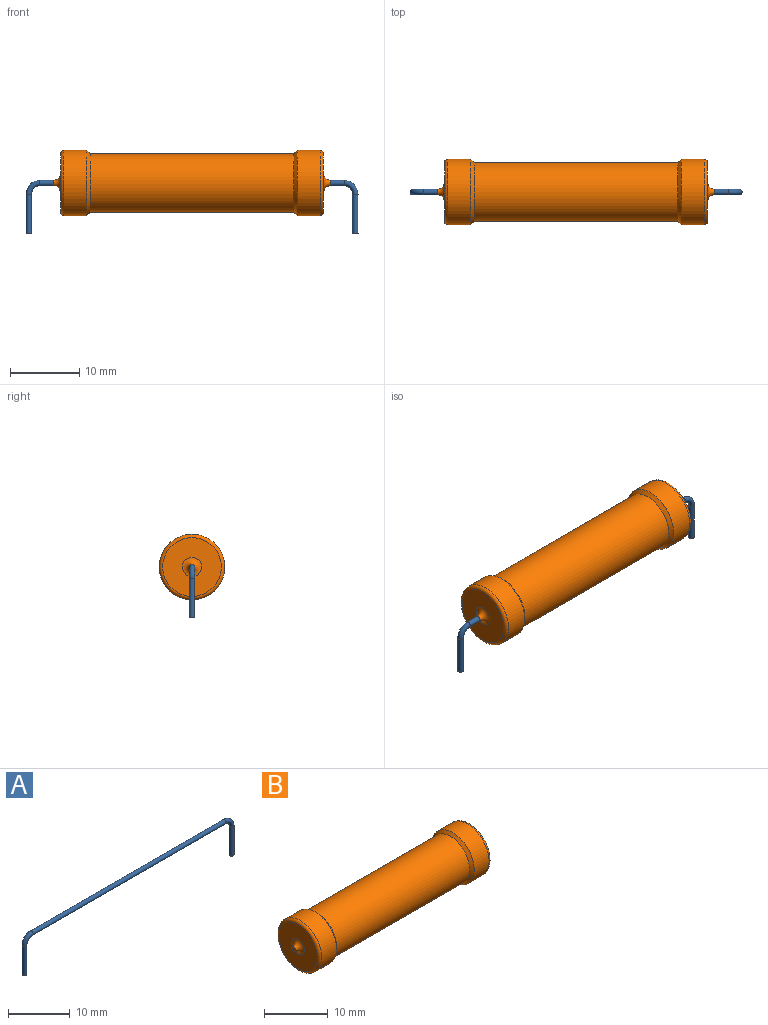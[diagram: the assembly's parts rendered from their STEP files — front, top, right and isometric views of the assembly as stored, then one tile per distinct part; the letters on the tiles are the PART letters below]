
ASSEMBLY  parts=2 mates=2
PART A: 7 faces, bbox 48.4x0.8x7.9 mm
  f0: plane 0.8x0.8mm, normal (0,0,-1), area 0.5mm2, adj f1
  f1: cylinder r=0.4mm len=5.75mm, axis (0,0,1), area 14.5mm2, adj f0,f2
  f2: torus R=1.6mm, axis (0,1,0), area 6.3mm2, adj f1,f3
  f3: cylinder r=0.4mm len=44.1mm, axis (1,0,0), area 110.8mm2, adj f2,f6
  f4: plane 0.8x0.8mm, normal (0,0,-1), area 0.5mm2, adj f5
  f5: cylinder r=0.4mm len=5.75mm, axis (0,0,1), area 14.5mm2, adj f4,f6
  f6: torus R=1.6mm, axis (0,1,0), area 6.3mm2, adj f3,f5
PART B: 13 faces, bbox 40.1x10.3x10.3 mm
  f0: cylinder r=4.75mm len=9.5mm, axis (-1,0,0), area 98.5mm2, adj f1,f6
  f1: torus R=4.25mm, axis (-1,0,0), area 22.5mm2, adj f0,f2
  f2: plane 8.5x8.5mm, normal (-1,0,0), area 50.6mm2, adj f1,f3
  f3: torus R=1.4mm, axis (-1,0,0), area 7.5mm2, adj f2,f4
  f4: plane 0.8x0.8mm, normal (-1,0,0), area 0.5mm2, adj f3
  f5: cylinder r=4.25mm len=29.5mm, axis (-1,0,0), area 787.8mm2, adj f6,f12
  f6: cone r=4.75mm half-angle=45deg, axis (-1,0,0), area 20mm2, adj f0,f5
  f7: cylinder r=4.75mm len=9.5mm, axis (1,0,0), area 98.5mm2, adj f8,f12
  f8: torus R=4.25mm, axis (1,0,0), area 22.5mm2, adj f7,f9
  f9: plane 8.5x8.5mm, normal (1,0,0), area 50.6mm2, adj f8,f10
  f10: torus R=1.4mm, axis (1,0,0), area 7.5mm2, adj f9,f11
  f11: plane 0.8x0.8mm, normal (1,0,0), area 0.5mm2, adj f10
  f12: cone r=4.75mm half-angle=45deg, axis (1,0,0), area 20mm2, adj f5,f7
PLACE A t=(0.03,0,-4.75)mm
PLACE B t=(0.03,0,-4.75)mm
MATE cylindrical B.f0 <-> A.f3  axis (-1,0,0) through (0.03,0,0)mm
MATE fastened B.f0 <-> A.f3  axis (1,0,0) through (20.08,0,0)mm
